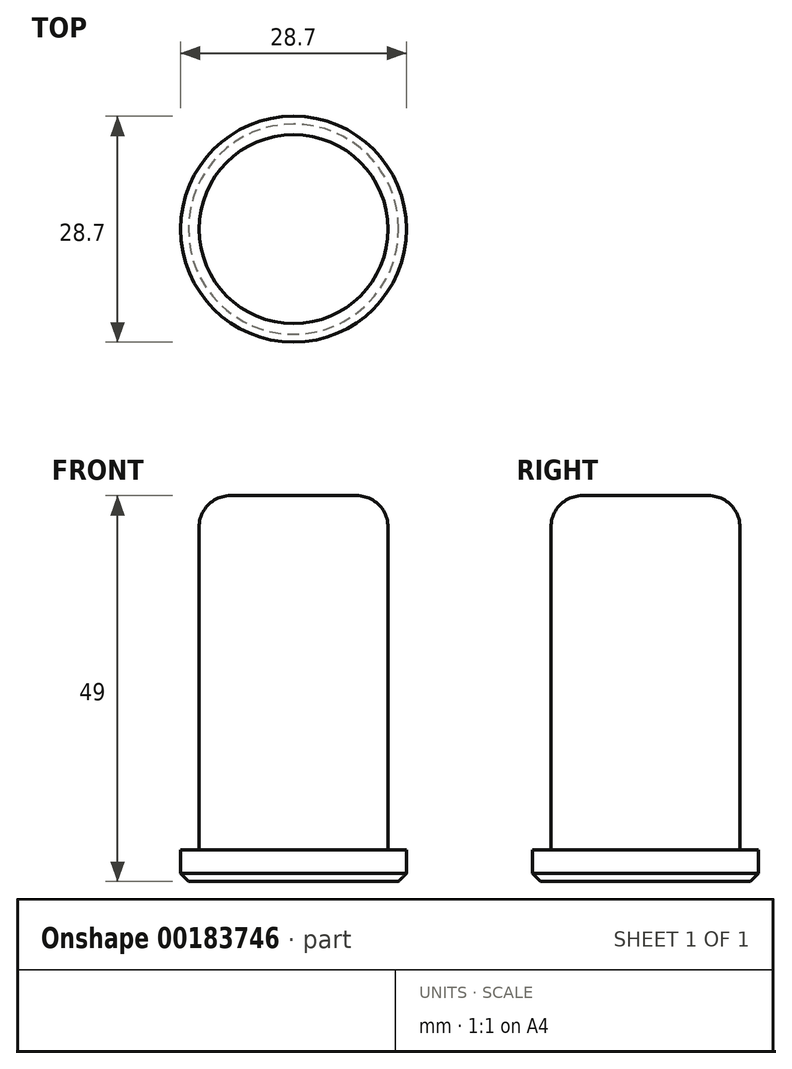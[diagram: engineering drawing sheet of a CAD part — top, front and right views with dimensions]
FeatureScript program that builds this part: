
annotation { "Feature Type Name" : "Feature", "Feature Type Description" : "" }
export const myFeature = defineFeature(function(context is Context, id is Id, definition is map)
    precondition{}
    {
        {
            var Q0;
            Q0=qCreatedBy(makeId("Top.planeOp"),FACE);
            var sketch = newSketch(context, id + "F0", { "sketchPlane" : qUnion([Q0])});
            skCircle(sketch, "E0", {"center": v(0, 0) * mm, "radius": 14.35 * mm});
            skSolve(sketch);
        }
        {
            var Q0;
            Q0 = qSketchRegion(id + "F0", true);
            extrude(context, id + "F1", {"entities" : qUnion([Q0]), "depth" : 4 * mm});
        }
        {
            var Q0;
            Q0=makeQuery(id+"F1.opExtrude","CAP_FACE",FACE,{"disambiguationData":[OSD([sQuery(id+"F0.wireOp",EDGE,"E0")])],"isStart":false});
            var sketch = newSketch(context, id + "F2", { "sketchPlane" : qUnion([Q0])});
            skCircle(sketch, "E1", {"center": v(0, 0) * mm, "radius": 12 * mm});
            skSolve(sketch);
        }
        {
            var Q0;
            Q0 = qSketchRegion(id + "F2", true);
            extrude(context, id + "F3", {"entities" : qUnion([Q0]), "operationType" : NewBodyOperationType.ADD, "depth" : 45 * mm});
        }
        {
            var Q0;
            Q0=makeQuery(id+"F3.opExtrude","CAP_EDGE",EDGE,{"disambiguationData":[OSD([sQuery(id+"F2.wireOp",EDGE,"E1")])],"isStart":false});
            fillet(context, id + "F4", {"entities" : qUnion([Q0]), "radius" : 4 * mm, "tangentPropagation" : true, "allowEdgeOverflow" : false});
        }
        {
            var Q0;
            Q0=makeQuery(id+"F1.opExtrude","CAP_EDGE",EDGE,{"disambiguationData":[OSD([sQuery(id+"F0.wireOp",EDGE,"E0")])],"isStart":true});
            chamfer(context, id + "F5", {"entities" : qUnion([Q0]), "width" : 1 * mm, "tangentPropagation" : true});
        }
    });
